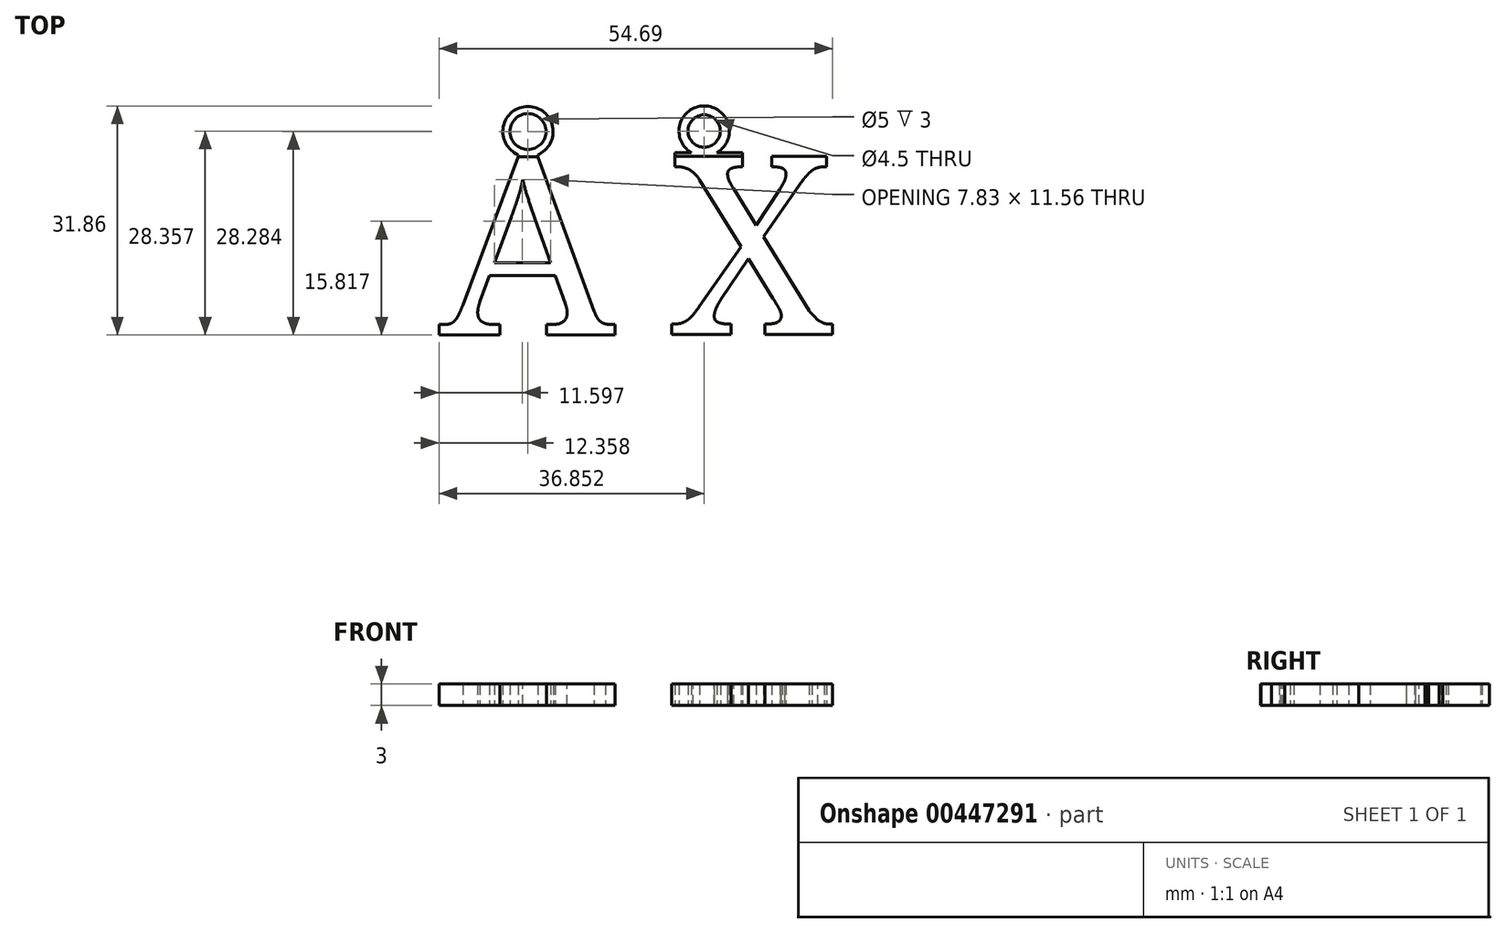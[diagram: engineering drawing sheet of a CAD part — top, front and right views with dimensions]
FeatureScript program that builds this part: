
annotation { "Feature Type Name" : "Feature", "Feature Type Description" : "" }
export const myFeature = defineFeature(function(context is Context, id is Id, definition is map)
    precondition{}
    {
        {
            var Q0;
            Q0=qCreatedBy(makeId("Top.planeOp"),FACE);
            var sketch = newSketch(context, id + "F0", { "sketchPlane" : qUnion([Q0])});
            skText(sketch, "E0", { "text": "X", "fontName": "NotoSerif-Regular.ttf"});
            skText(sketch, "E1", { "text": "A", "fontName": "NotoSerif-Regular.ttf"});
            const initialGuessF0  = {"E0": [0.00783, -0.0263, 1, 0, 0.025], "E1": [-0.02423, -0.02636, 1, 0, 0.025]};
            skSetInitialGuess(sketch, initialGuessF0);
            skSolve(sketch);
        }
        {
            var Q0;
            Q0 = qSketchRegion(id + "F0", true);
            extrude(context, id + "F1", {"entities" : qUnion([Q0]), "depth" : 3 * mm});
        }
        {
            var Q0;
            Q0=qCreatedBy(makeId("Top.planeOp"),FACE);
            var sketch = newSketch(context, id + "F2", { "sketchPlane" : qUnion([Q0])});
            skLineSegment(sketch, "E2", {"start": v(-11.87, -1.58) * mm, "end": v(-11.87, -1.58) * mm});
            skCircle(sketch, "E3", {"center": v(-11.87, 1.92) * mm, "radius": 2.5 * mm});
            skLineSegment(sketch, "E4.bottom", {"start": v(-13.23, -1.58) * mm, "end": v(-10.52, -1.58) * mm});
            skLineSegment(sketch, "E4.left", {"start": v(-13.23, -1.58) * mm, "end": v(-13.23, -1.3) * mm});
            skLineSegment(sketch, "E4.right", {"start": v(-10.52, -1.58) * mm, "end": v(-10.52, -1.3) * mm});
            skArc(sketch, "E5.trimOffspring", {"start": v(-10.52, -1.3) * mm, "mid": v(-11.87, 5.42) * mm, "end": v(-13.23, -1.3) * mm});
            skCircle(sketch, "E6", {"center": v(12.62, 2) * mm, "radius": 2.25 * mm});
            skCircle(sketch, "E7", {"center": v(12.62, 2) * mm, "radius": 3.5 * mm});
            skLineSegment(sketch, "E8.bottom", {"start": v(8.55, -1.5) * mm, "end": v(17.97, -1.5) * mm});
            skLineSegment(sketch, "E9", {"start": v(8.55, -1.5) * mm, "end": v(8.55, -1) * mm});
            skLineSegment(sketch, "E10", {"start": v(8.55, -1) * mm, "end": v(17.97, -1) * mm});
            skLineSegment(sketch, "E11", {"start": v(17.97, -1) * mm, "end": v(17.97, -1.5) * mm});
            skSolve(sketch);
        }
        {
            var Q0;
            Q0 = qSketchRegion(id + "F2", true);
            extrude(context, id + "F3", {"entities" : qUnion([Q0]), "depth" : 3 * mm});
        }
    });
